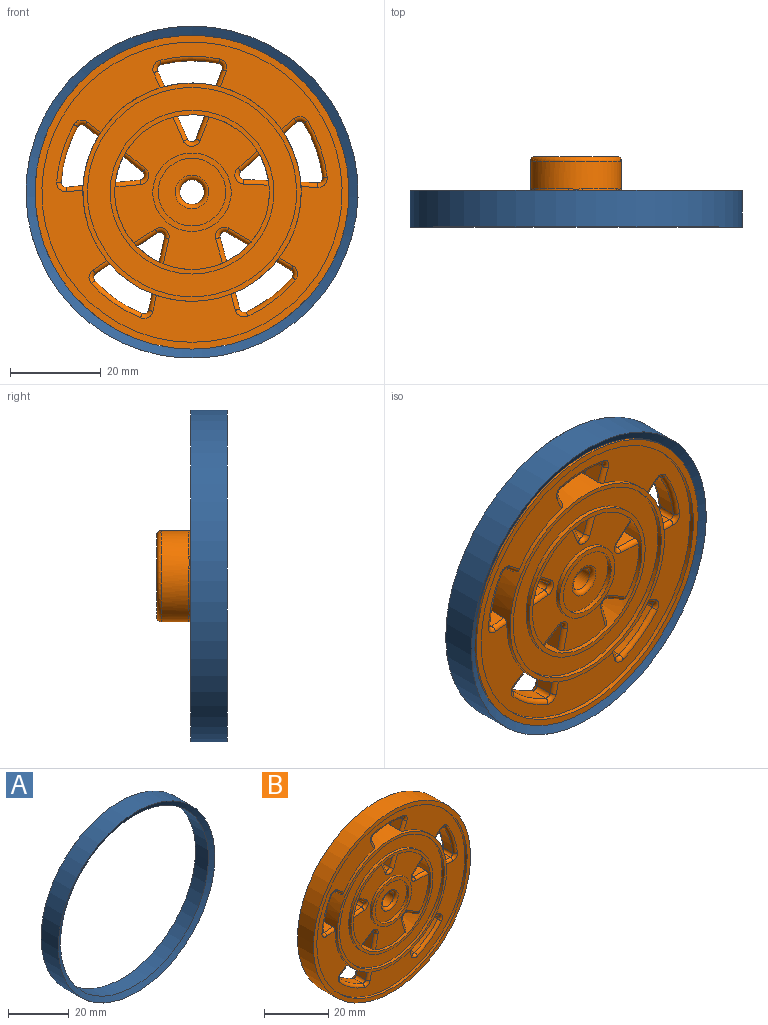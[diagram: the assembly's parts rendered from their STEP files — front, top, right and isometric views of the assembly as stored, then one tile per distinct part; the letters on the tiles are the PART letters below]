
ASSEMBLY  parts=2 mates=1
PART A: 6 faces, bbox 73x8x73 mm
  f0: cone r=36.5mm half-angle=63.4deg, axis (0,1,0), area 498.8mm2, adj f1,f5
  f1: plane 73.02x73.02mm, normal (0,1,0), area 1.9mm2, adj f0,f2
  f2: cylinder r=36.51mm len=73.02mm, axis (0,1,0), area 1835.1mm2, adj f1,f3
  f3: plane 73.02x73.02mm, normal (0,-1,0), area 1.9mm2, adj f2,f4
  f4: cone r=34.5mm half-angle=63.4deg, axis (0,-1,0), area 498.8mm2, adj f3,f5
  f5: cylinder r=34.5mm len=69mm, axis (0,1,0), area 1300.6mm2, adj f0,f4
PART B: 154 faces, bbox 69x15x69 mm
  f0: plane 14.84x14.84mm, normal (0,-1,0), area 130.1mm2, adj f140,f149
  f1: plane 46x46mm, normal (0,-1,0), area 644mm2, adj f145,f147
  f2: plane 34x33.58mm, normal (0,-1,0), area 492.2mm2, adj f110,f111,f112,f116,f117,f118,f122,f123
  f3: plane 4x3.56mm, normal (-0.94,0,0.35), area 15.2mm2, adj f16,f23,f62,f144
  f4: plane 4x3.42mm, normal (0.92,0,0.4), area 14.9mm2, adj f15,f24,f63,f144
  f5: plane 4x3.8mm, normal (0.05,0,1), area 15.2mm2, adj f14,f25,f61,f144
  f6: plane 4x2.79mm, normal (0.66,0,-0.75), area 14.9mm2, adj f13,f26,f60,f144
  f7: plane 4x3.66mm, normal (0.96,0,0.27), area 15.2mm2, adj f18,f27,f58,f144
  f8: plane 4x3.21mm, normal (-0.51,0,-0.86), area 14.9mm2, adj f17,f28,f59,f144
  f9: plane 4x3.17mm, normal (0.55,0,-0.83), area 15.2mm2, adj f20,f29,f56,f144
  f10: plane 4x3.64mm, normal (-0.98,0,0.22), area 14.9mm2, adj f19,f30,f57,f144
  f11: plane 4x2.97mm, normal (-0.62,0,-0.78), area 15.2mm2, adj f22,f31,f54,f144
  f12: plane 4x3.71mm, normal (-0.1,0,1), area 14.9mm2, adj f21,f32,f55,f144
  f13: cylinder r=1mm len=3.45mm, axis (0.75,0,0.66), area 5.7mm2, adj f6,f35,f69,f144
  f14: cylinder r=1mm len=3.84mm, axis (-1,0,0.05), area 5.9mm2, adj f5,f35,f73,f144
  f15: cylinder r=1mm len=3.82mm, axis (-0.4,0,0.92), area 5.7mm2, adj f4,f35,f76,f144
  f16: cylinder r=1mm len=3.91mm, axis (-0.35,0,-0.94), area 5.9mm2, adj f3,f35,f77,f143
  f17: cylinder r=1mm len=3.72mm, axis (0.86,0,-0.51), area 5.7mm2, adj f8,f35,f82,f144
  f18: cylinder r=1mm len=3.93mm, axis (-0.27,0,0.96), area 5.9mm2, adj f7,f35,f83,f144
  f19: cylinder r=1mm len=3.86mm, axis (-0.22,0,-0.98), area 5.7mm2, adj f10,f35,f88,f144
  f20: cylinder r=1mm len=3.72mm, axis (0.83,0,0.55), area 5.9mm2, adj f9,f35,f89,f144
  f21: cylinder r=1mm len=3.81mm, axis (-1,0,-0.1), area 5.7mm2, adj f12,f35,f94,f144
  f22: cylinder r=1mm len=3.59mm, axis (0.78,0,-0.62), area 5.9mm2, adj f11,f35,f95,f144
  f23: cylinder r=1mm len=3.91mm, axis (-0.35,0,-0.94), area 5.9mm2, adj f3,f33,f113,f144
  f24: cylinder r=1mm len=3.82mm, axis (-0.4,0,0.92), area 5.7mm2, adj f4,f33,f114,f144
  f25: cylinder r=1mm len=3.84mm, axis (-1,0,0.05), area 5.9mm2, adj f5,f33,f119,f144
  f26: cylinder r=1mm len=3.45mm, axis (0.75,0,0.66), area 5.7mm2, adj f6,f33,f120,f144
  f27: cylinder r=1mm len=3.93mm, axis (-0.27,0,0.96), area 5.9mm2, adj f7,f33,f125,f144
  f28: cylinder r=1mm len=3.72mm, axis (0.86,0,-0.51), area 5.7mm2, adj f8,f33,f126,f144
  f29: cylinder r=1mm len=3.72mm, axis (0.83,0,0.55), area 5.9mm2, adj f9,f33,f131,f144
  f30: cylinder r=1mm len=3.86mm, axis (-0.22,0,-0.98), area 5.7mm2, adj f10,f33,f132,f144
  f31: cylinder r=1mm len=3.59mm, axis (0.78,0,-0.62), area 5.9mm2, adj f11,f33,f137,f144
  f32: cylinder r=1mm len=3.81mm, axis (-1,0,-0.1), area 5.7mm2, adj f12,f33,f138,f144
  f33: plane 66x66mm, normal (0,-1,0), area 1162.5mm2, adj f23,f24,f25,f26,f27,f28,f29,f30
  f34: cylinder r=34.5mm len=69mm, axis (0,1,0), area 1517.4mm2, adj f35,f153
  f35: plane 69x69mm, normal (0,1,0), area 2738.7mm2, adj f13,f14,f15,f16,f17,f18,f19,f20
  f36: cylinder r=10mm len=20mm, axis (0,-1,0), area 378.7mm2, adj f99,f100,f101,f102,f103,f104,f105,f106
  f37: plane 18x18mm, normal (0,1,0), area 231.6mm2, adj f38,f109
  f38: cylinder r=2.7mm len=13mm, axis (0,1,0), area 220.5mm2, adj f37,f140
  f39: cylinder r=28.91mm len=12.72mm, axis (0,1,0), area 51.3mm2, adj f62,f63,f75,f115
  f40: plane 5.09x4mm, normal (-0.94,0,0.35), area 21.7mm2, adj f68,f79,f111,f141
  f41: plane 5.06x4mm, normal (0.92,0,0.4), area 22.1mm2, adj f68,f78,f112,f141
  f42: plane 5.43x4mm, normal (0.05,0,1), area 21.7mm2, adj f67,f74,f117,f141
  f43: plane 4.13x4mm, normal (0.66,0,-0.75), area 22.1mm2, adj f67,f70,f118,f141
  f44: cylinder r=28.91mm len=12.01mm, axis (0,1,0), area 51.3mm2, adj f60,f61,f71,f121
  f45: plane 5.24x4mm, normal (0.96,0,0.27), area 21.7mm2, adj f66,f85,f123,f141
  f46: plane 4.76x4mm, normal (-0.51,0,-0.86), area 22.1mm2, adj f66,f84,f124,f141
  f47: cylinder r=28.91mm len=10.13mm, axis (0,1,0), area 51.3mm2, adj f58,f59,f81,f127
  f48: plane 4.54x4mm, normal (0.55,0,-0.83), area 21.7mm2, adj f65,f91,f129,f141
  f49: plane 5.39x4mm, normal (-0.98,0,0.22), area 22.1mm2, adj f65,f90,f130,f141
  f50: cylinder r=28.91mm len=10.46mm, axis (0,1,0), area 51.3mm2, adj f56,f57,f87,f133
  f51: plane 4.25x4mm, normal (-0.62,0,-0.78), area 21.7mm2, adj f64,f97,f135,f141
  f52: plane 5.49x4mm, normal (-0.1,0,1), area 22.1mm2, adj f64,f96,f136,f141
  f53: cylinder r=28.91mm len=12.19mm, axis (0,1,0), area 51.3mm2, adj f54,f55,f93,f139
  f54: cylinder r=1mm len=4mm, axis (0,1,0), area 6.9mm2, adj f11,f53,f95,f137
  f55: cylinder r=1mm len=4mm, axis (0,1,0), area 6.9mm2, adj f12,f53,f94,f138
  f56: cylinder r=1mm len=4mm, axis (0,1,0), area 6.9mm2, adj f9,f50,f89,f131
  f57: cylinder r=1mm len=4mm, axis (0,1,0), area 6.9mm2, adj f10,f50,f88,f132
  f58: cylinder r=1mm len=4mm, axis (0,1,0), area 6.9mm2, adj f7,f47,f83,f125
  f59: cylinder r=1mm len=4mm, axis (0,1,0), area 6.9mm2, adj f8,f47,f82,f126
  f60: cylinder r=1mm len=4mm, axis (0,1,0), area 6.9mm2, adj f6,f44,f69,f120
  f61: cylinder r=1mm len=4mm, axis (0,1,0), area 6.9mm2, adj f5,f44,f73,f119
  f62: cylinder r=1mm len=4mm, axis (0,1,0), area 6.9mm2, adj f3,f39,f77,f113
  f63: cylinder r=1mm len=4mm, axis (0,1,0), area 6.9mm2, adj f4,f39,f76,f114
  f64: cylinder r=1mm len=4mm, axis (0,-1,0), area 9.5mm2, adj f51,f52,f98,f134
  f65: cylinder r=1mm len=4mm, axis (0,-1,0), area 9.5mm2, adj f48,f49,f92,f128
  f66: cylinder r=1mm len=4mm, axis (0,-1,0), area 9.5mm2, adj f45,f46,f86,f122
  f67: cylinder r=1mm len=4mm, axis (0,-1,0), area 9.5mm2, adj f42,f43,f72,f116
  f68: cylinder r=1mm len=4mm, axis (0,-1,0), area 9.5mm2, adj f40,f41,f80,f110
  f69: torus R=2mm, axis (0,-1,0), area 3.7mm2, adj f13,f35,f60,f71
  f70: cylinder r=1mm len=4.94mm, axis (0.75,0,0.66), area 8.8mm2, adj f35,f43,f72,f141
  f71: torus R=29.91mm, axis (0,-1,0), area 20.4mm2, adj f35,f44,f69,f73
  f72: torus R=2mm, axis (0,-1,0), area 3.8mm2, adj f35,f67,f70,f74,f101
  f73: torus R=2mm, axis (0,-1,0), area 3.7mm2, adj f14,f35,f61,f71
  f74: cylinder r=1mm len=5.64mm, axis (-1,0,0.05), area 8.7mm2, adj f35,f42,f72,f141
  f75: torus R=29.91mm, axis (0,-1,0), area 20.4mm2, adj f35,f39,f76,f77
  f76: torus R=2mm, axis (0,-1,0), area 3.7mm2, adj f15,f35,f63,f75
  f77: torus R=2mm, axis (0,-1,0), area 3.7mm2, adj f16,f35,f62,f75
  f78: cylinder r=1mm len=5.64mm, axis (-0.4,0,0.92), area 8.8mm2, adj f35,f41,f80,f141
  f79: cylinder r=1mm len=5.6mm, axis (-0.35,0,-0.94), area 8.7mm2, adj f35,f40,f80,f142
  f80: torus R=2mm, axis (0,-1,0), area 3.8mm2, adj f35,f68,f78,f79,f105
  f81: torus R=29.91mm, axis (0,-1,0), area 20.4mm2, adj f35,f47,f82,f83
  f82: torus R=2mm, axis (0,-1,0), area 3.7mm2, adj f17,f35,f59,f81
  f83: torus R=2mm, axis (0,-1,0), area 3.7mm2, adj f18,f35,f58,f81
  f84: cylinder r=1mm len=5.43mm, axis (0.86,0,-0.51), area 8.8mm2, adj f35,f46,f86,f141
  f85: cylinder r=1mm len=5.67mm, axis (-0.27,0,0.96), area 8.7mm2, adj f35,f45,f86,f141
  f86: torus R=2mm, axis (0,-1,0), area 3.8mm2, adj f35,f66,f84,f85,f100
  f87: torus R=29.91mm, axis (0,-1,0), area 20.4mm2, adj f35,f50,f88,f89
  f88: torus R=2mm, axis (0,-1,0), area 3.7mm2, adj f19,f35,f57,f87
  f89: torus R=2mm, axis (0,-1,0), area 3.7mm2, adj f20,f35,f56,f87
  f90: cylinder r=1mm len=5.8mm, axis (-0.22,0,-0.98), area 8.8mm2, adj f35,f49,f92,f141
  f91: cylinder r=1mm len=5.23mm, axis (0.83,0,0.55), area 8.7mm2, adj f35,f48,f92,f141
  f92: torus R=2mm, axis (0,-1,0), area 3.8mm2, adj f35,f65,f90,f91,f104
  f93: torus R=29.91mm, axis (0,-1,0), area 20.4mm2, adj f35,f53,f94,f95
  f94: torus R=2mm, axis (0,-1,0), area 3.7mm2, adj f21,f35,f55,f93
  f95: torus R=2mm, axis (0,-1,0), area 3.7mm2, adj f22,f35,f54,f93
  f96: cylinder r=1mm len=5.78mm, axis (-1,0,-0.1), area 8.8mm2, adj f35,f52,f98,f141
  f97: cylinder r=1mm len=5mm, axis (0.78,0,-0.62), area 8.7mm2, adj f35,f51,f98,f141
  f98: torus R=2mm, axis (0,-1,0), area 3.8mm2, adj f35,f64,f96,f97,f108
  f99: torus R=11mm, axis (0,-1,0), area 15.6mm2, adj f35,f36,f100,f101
  f100: bspline ~3.45x3.03mm, area 3.9mm2, adj f36,f86,f99,f102
  f101: bspline ~4.01x2.26mm, area 3.9mm2, adj f36,f72,f99,f103
  f102: torus R=11mm, axis (0,-1,0), area 15.6mm2, adj f35,f36,f100,f104
  f103: torus R=11mm, axis (0,-1,0), area 15.6mm2, adj f35,f36,f101,f105
  f104: bspline ~3.77x3.14mm, area 3.9mm2, adj f36,f92,f102,f106
  f105: bspline ~3.64x1.12mm, area 3.9mm2, adj f36,f80,f103,f107
  f106: torus R=11mm, axis (0,-1,0), area 15.6mm2, adj f35,f36,f104,f108
  f107: torus R=11mm, axis (0,-1,0), area 15.6mm2, adj f35,f36,f105,f108
  f108: bspline ~4.01x2.22mm, area 3.9mm2, adj f36,f98,f106,f107
  f109: torus R=9mm, axis (0,1,0), area 95.1mm2, adj f36,f37
  f110: torus R=2mm, axis (0,-1,0), area 5.1mm2, adj f2,f68,f111,f112
  f111: cylinder r=1mm len=5.6mm, axis (-0.35,0,-0.94), area 8.7mm2, adj f2,f40,f110,f141
  f112: cylinder r=1mm len=5.64mm, axis (-0.4,0,0.92), area 8.8mm2, adj f2,f41,f110,f141
  f113: torus R=2mm, axis (0,-1,0), area 3.7mm2, adj f23,f33,f62,f115
  f114: torus R=2mm, axis (0,-1,0), area 3.7mm2, adj f24,f33,f63,f115
  f115: torus R=29.91mm, axis (0,-1,0), area 20.4mm2, adj f33,f39,f113,f114
  f116: torus R=2mm, axis (0,-1,0), area 5.1mm2, adj f2,f67,f117,f118
  f117: cylinder r=1mm len=5.64mm, axis (-1,0,0.05), area 8.7mm2, adj f2,f42,f116,f141
  f118: cylinder r=1mm len=4.94mm, axis (0.75,0,0.66), area 8.8mm2, adj f2,f43,f116,f141
  f119: torus R=2mm, axis (0,-1,0), area 3.7mm2, adj f25,f33,f61,f121
  f120: torus R=2mm, axis (0,-1,0), area 3.7mm2, adj f26,f33,f60,f121
  f121: torus R=29.91mm, axis (0,-1,0), area 20.4mm2, adj f33,f44,f119,f120
  f122: torus R=2mm, axis (0,-1,0), area 5.1mm2, adj f2,f66,f123,f124
  f123: cylinder r=1mm len=5.67mm, axis (-0.27,0,0.96), area 8.7mm2, adj f2,f45,f122,f141
  f124: cylinder r=1mm len=5.43mm, axis (0.86,0,-0.51), area 8.8mm2, adj f2,f46,f122,f141
  f125: torus R=2mm, axis (0,-1,0), area 3.7mm2, adj f27,f33,f58,f127
  f126: torus R=2mm, axis (0,-1,0), area 3.7mm2, adj f28,f33,f59,f127
  f127: torus R=29.91mm, axis (0,-1,0), area 20.4mm2, adj f33,f47,f125,f126
  f128: torus R=2mm, axis (0,-1,0), area 5.1mm2, adj f2,f65,f129,f130
  f129: cylinder r=1mm len=5.23mm, axis (0.83,0,0.55), area 8.7mm2, adj f2,f48,f128,f141
  f130: cylinder r=1mm len=5.8mm, axis (-0.22,0,-0.98), area 8.8mm2, adj f2,f49,f128,f141
  f131: torus R=2mm, axis (0,-1,0), area 3.7mm2, adj f29,f33,f56,f133
  f132: torus R=2mm, axis (0,-1,0), area 3.7mm2, adj f30,f33,f57,f133
  f133: torus R=29.91mm, axis (0,-1,0), area 20.4mm2, adj f33,f50,f131,f132
  f134: torus R=2mm, axis (0,-1,0), area 5.1mm2, adj f2,f64,f135,f136
  f135: cylinder r=1mm len=5mm, axis (0.78,0,-0.62), area 8.7mm2, adj f2,f51,f134,f141
  f136: cylinder r=1mm len=5.78mm, axis (-1,0,-0.1), area 8.8mm2, adj f2,f52,f134,f141
  f137: torus R=2mm, axis (0,-1,0), area 3.7mm2, adj f31,f33,f54,f139
  f138: torus R=2mm, axis (0,-1,0), area 3.7mm2, adj f32,f33,f55,f139
  f139: torus R=29.91mm, axis (0,-1,0), area 20.4mm2, adj f33,f53,f137,f138
  f140: torus R=3.7mm, axis (0,-1,0), area 30.2mm2, adj f0,f38
  f141: cylinder r=17mm len=34mm, axis (0,1,0), area 291mm2, adj f2,f35,f40,f41,f42,f43,f45,f46
  f142: cylinder r=17mm len=1mm, axis (0,1,0), area 0.2mm2, adj f35,f79,f141
  f143: cylinder r=24mm len=1mm, axis (0,1,0), area 0.2mm2, adj f16,f35,f144
  f144: cylinder r=24mm len=48mm, axis (0,1,0), area 497.4mm2, adj f3,f4,f5,f6,f7,f8,f9,f10
  f145: cylinder r=18mm len=36mm, axis (0,1,0), area 113.1mm2, adj f1,f146
  f146: plane 36x36mm, normal (0,-1,0), area 110mm2, adj f141,f145
  f147: cylinder r=23mm len=46mm, axis (0,1,0), area 144.5mm2, adj f1,f148
  f148: plane 48x48mm, normal (0,-1,0), area 147.7mm2, adj f144,f147
  f149: cylinder r=7.42mm len=14.84mm, axis (0,1,0), area 46.6mm2, adj f0,f151
  f150: cylinder r=8.62mm len=17.24mm, axis (0,1,0), area 54.2mm2, adj f2,f151
  f151: plane 17.24x17.24mm, normal (0,-1,0), area 60.5mm2, adj f149,f150
  f152: cylinder r=33mm len=66mm, axis (0,1,0), area 207.3mm2, adj f33,f153
  f153: plane 69x69mm, normal (0,-1,0), area 318.1mm2, adj f34,f152
PLACE A t=(0,-1.5,-5.5)mm
PLACE B t=(0,32.15,3.2)mm
MATE fastened B.f34 <-> A.f4  axis (0,1,0) through (0,28.65,3.2)mm
